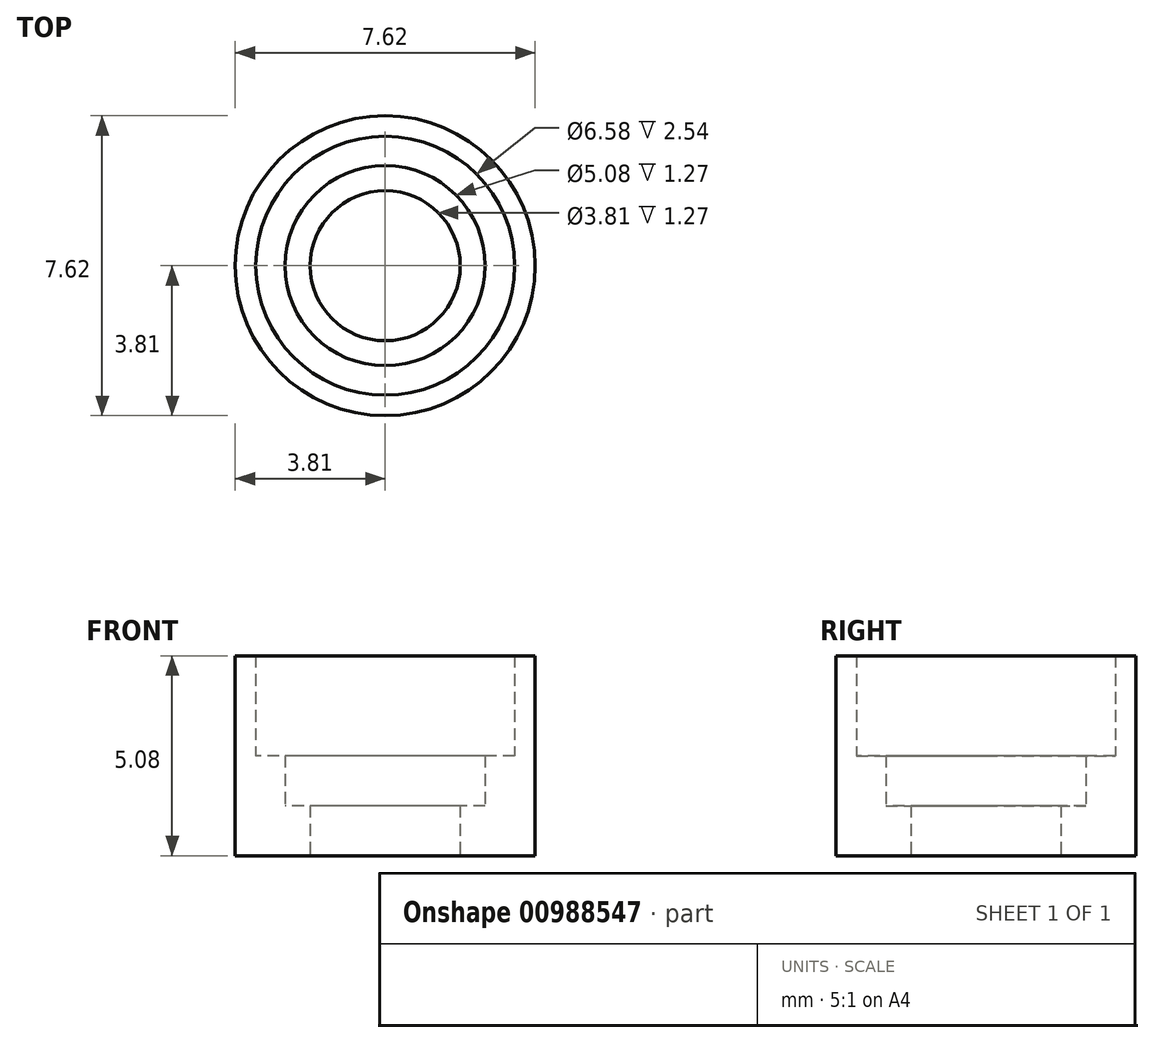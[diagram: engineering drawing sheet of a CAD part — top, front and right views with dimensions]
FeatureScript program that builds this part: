
annotation { "Feature Type Name" : "Feature", "Feature Type Description" : "" }
export const myFeature = defineFeature(function(context is Context, id is Id, definition is map)
    precondition{}
    {
        {
            var Q0;
            Q0=qCreatedBy(makeId("Top.planeOp"),FACE);
            var sketch = newSketch(context, id + "F0", { "sketchPlane" : qUnion([Q0])});
            skCircle(sketch, "E0", {"center": v(0, 0) * mm, "radius": 3.29 * mm});
            skCircle(sketch, "E1", {"center": v(0, 0) * mm, "radius": 1.9 * mm});
            skCircle(sketch, "E2", {"center": v(0, 0) * mm, "radius": 3.81 * mm});
            skCircle(sketch, "E3", {"center": v(0, 0) * mm, "radius": 2.54 * mm});
            skSolve(sketch);
        }
        {
            var Q0;
            Q0 = qSketchRegion(id + "F0", true);
            extrude(context, id + "F1", {"entities" : qUnion([Q0]), "depth" : 5.08 * mm, "offsetDistance" : 25.4 * mm});
        }
        {
            var Q0;
            Q0=makeQuery(id+"F0.imprint","IMPRINT",FACE,{"disambiguationData":[TD([[makeQuery(id+"F0.imprint","IMPRINT",EDGE,{"derivedFrom":sQuery(id+"F0.wireOp",EDGE,"E0")}),1.0]])]});
            extrude(context, id + "F2", {"entities" : qUnion([Q0]), "operationType" : NewBodyOperationType.ADD, "depth" : 2.54 * mm, "offsetDistance" : 25.4 * mm});
        }
        {
            var Q0;
            Q0=makeQuery(id+"F0.imprint","IMPRINT",FACE,{"disambiguationData":[TD([[makeQuery(id+"F0.imprint","IMPRINT",EDGE,{"derivedFrom":sQuery(id+"F0.wireOp",EDGE,"E1")}),-1.0]])]});
            extrude(context, id + "F3", {"entities" : qUnion([Q0]), "operationType" : NewBodyOperationType.ADD, "depth" : 1.27 * mm, "offsetDistance" : 25.4 * mm});
        }
    });
